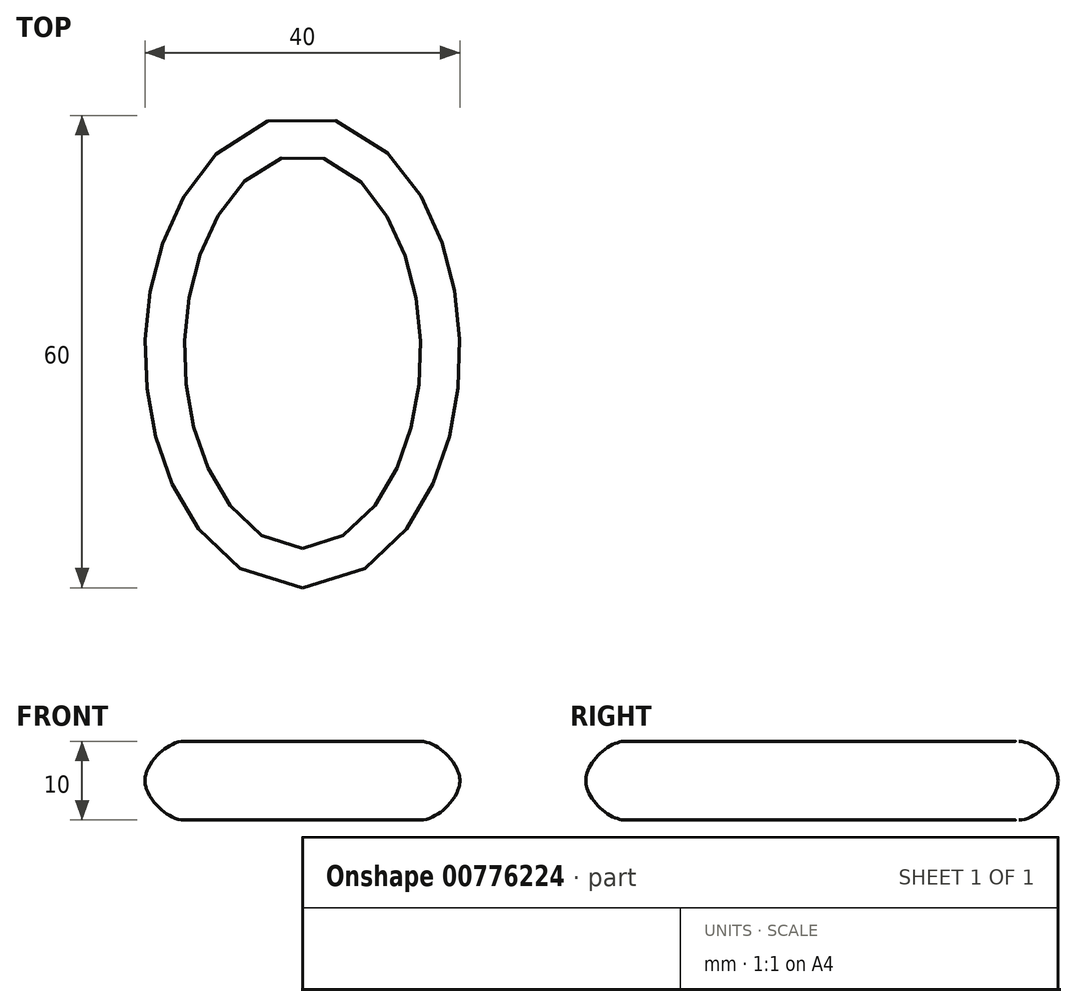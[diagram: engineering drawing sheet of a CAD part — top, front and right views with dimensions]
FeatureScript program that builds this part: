
annotation { "Feature Type Name" : "Feature", "Feature Type Description" : "" }
export const myFeature = defineFeature(function(context is Context, id is Id, definition is map)
    precondition{}
    {
        {
            var Q0;
            Q0=qCreatedBy(makeId("Top.planeOp"),FACE);
            var sketch = newSketch(context, id + "F0", { "sketchPlane" : qUnion([Q0])});
            skEllipse(sketch, "E0", {"center": v(0, 0) * mm, "majorRadius": 30 * mm, "minorRadius": 20 * mm, "majorAxis": v(0, -1)});
            skSolve(sketch);
        }
        {
            var Q0;
            Q0=makeQuery(id+"F0.imprint","IMPRINT",FACE,{"disambiguationData":[TD([[makeQuery(id+"F0.imprint","IMPRINT",EDGE,{"derivedFrom":sQuery(id+"F0.wireOp",EDGE,"E0")}),1.0]])]});
            extrude(context, id + "F1", {"entities" : qUnion([Q0]), "depth" : 10 * mm, "offsetDistance" : 25 * mm});
        }
        {
            var Q0;
            Q0=makeQuery(id+"F1.opExtrude","CAP_FACE",FACE,{"disambiguationData":[OSD([sQuery(id+"F0.wireOp",EDGE,"E0")])],"isStart":false});
            var Q1;
            Q1=makeQuery(id+"F1.opExtrude","CAP_FACE",FACE,{"disambiguationData":[OSD([sQuery(id+"F0.wireOp",EDGE,"E0")])],"isStart":true});
            fillet(context, id + "F2", {"entities" : qUnion([Q0, Q1]), "radius" : 5 * mm, "rho" : .33, "crossSection" : FilletCrossSection.CONIC, "allowEdgeOverflow" : false});
        }
    });
